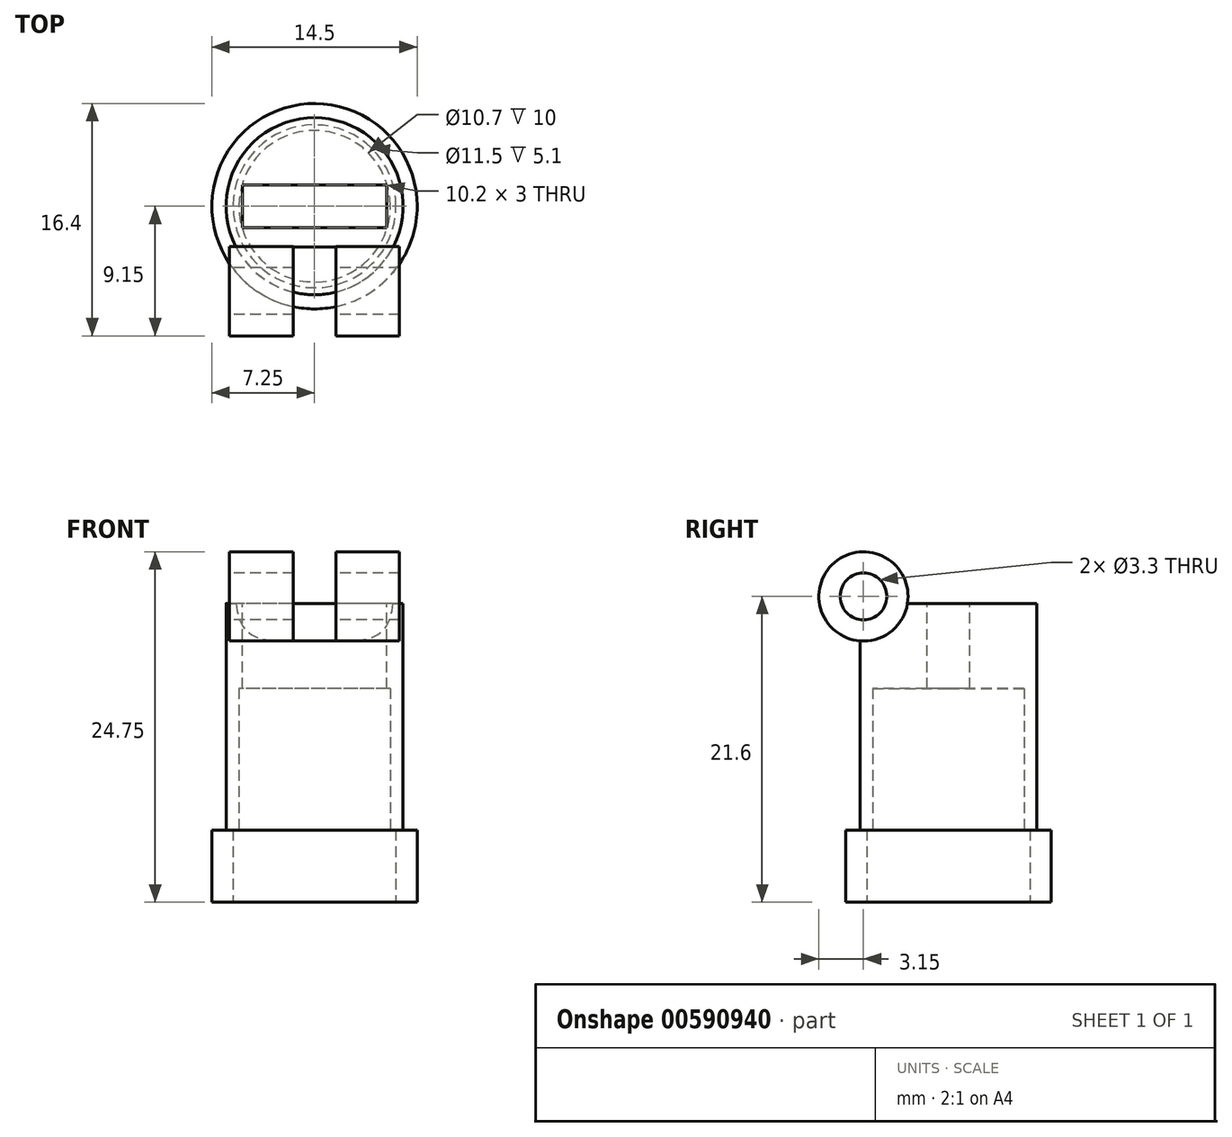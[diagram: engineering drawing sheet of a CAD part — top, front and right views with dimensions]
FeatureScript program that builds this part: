
annotation { "Feature Type Name" : "Feature", "Feature Type Description" : "" }
export const myFeature = defineFeature(function(context is Context, id is Id, definition is map)
    precondition{}
    {
        {
            var Q0;
            Q0=qCreatedBy(makeId("Top.planeOp"),FACE);
            var sketch = newSketch(context, id + "F0", { "sketchPlane" : qUnion([Q0])});
            skCircle(sketch, "E0", {"center": v(0, 0) * mm, "radius": 5.75 * mm});
            skCircle(sketch, "E1.0", {"center": v(0, 0) * mm, "radius": 7.25 * mm});
            skSolve(sketch);
        }
        {
            var Q0;
            Q0=makeQuery(id+"F0.imprint","IMPRINT",FACE,{"disambiguationData":[TD([[makeQuery(id+"F0.imprint","IMPRINT",EDGE,{"derivedFrom":sQuery(id+"F0.wireOp",EDGE,"E0")}),-1.0]])]});
            extrude(context, id + "F1", {"entities" : qUnion([Q0]), "depth" : 5.1 * mm, "offsetDistance" : 25 * mm});
        }
        {
            var Q0;
            Q0=makeQuery(id+"F1.opExtrude","CAP_FACE",FACE,{"disambiguationData":[OSD([sQuery(id+"F0.wireOp",EDGE,"E0"),sQuery(id+"F0.wireOp",EDGE,"E1.0")])],"isStart":false});
            var sketch = newSketch(context, id + "F2", { "sketchPlane" : qUnion([Q0])});
            skCircle(sketch, "E2.0", {"center": v(0, 0) * mm, "radius": 5.35 * mm});
            skCircle(sketch, "E3.0", {"center": v(0, 0) * mm, "radius": 6.25 * mm});
            skSolve(sketch);
        }
        {
            var Q0;
            Q0=makeQuery(id+"F2.imprint","IMPRINT",FACE,{"disambiguationData":[TD([[makeQuery(id+"F2.imprint","IMPRINT",EDGE,{"derivedFrom":sQuery(id+"F2.wireOp",EDGE,"E3.0")}),1.0]])]});
            var Q1;
            Q1=makeQuery(id+"F2.imprint","IMPRINT",FACE,{"disambiguationData":[TD([[makeQuery(id+"F2.imprint","IMPRINT",EDGE,{"derivedFrom":sQuery(id+"F2.wireOp",EDGE,"E2.0")}),-1.0]])]});
            extrude(context, id + "F3", {"entities" : qUnion([Q0, Q1]), "depth" : 16 * mm, "offsetDistance" : 25 * mm});
        }
        {
            var Q0;
            Q0=makeQuery(id+"F3.opExtrude","CAP_FACE",FACE,{"disambiguationData":[OSD([sQuery(id+"F0.wireOp",EDGE,"E0"),sQuery(id+"F2.wireOp",EDGE,"E2.0")])],"isStart":false});
            var sketch = newSketch(context, id + "F4", { "sketchPlane" : qUnion([Q0])});
            skCircle(sketch, "E4.0", {"center": v(0, 0) * mm, "radius": 0.6 * mm});
            skSolve(sketch);
        }
        {
            var Q0;
            Q0=makeQuery(id+"F4.imprint","IMPRINT",FACE,{"disambiguationData":[TD([[makeQuery(id+"F4.imprint","IMPRINT",EDGE,{"derivedFrom":sQuery(id+"F4.wireOp",EDGE,"E4.0")}),-1.0]])]});
            extrude(context, id + "F5", {"entities" : qUnion([Q0]), "operationType" : NewBodyOperationType.ADD, "oppositeDirection" : true, "depth" : 6 * mm, "offsetDistance" : 25 * mm});
        }
        {
            var Q0;
            {var subQ0=sQuery(id+"F2.wireOp",EDGE,"E2.0");Q0=makeQuery(id+"F5.boolean.opBoolean","MERGE",FACE,{"derivedFrom":[makeQuery(id+"F3.opExtrude","CAP_FACE",FACE,{"disambiguationData":[OSD([sQuery(id+"F0.wireOp",EDGE,"E0"),subQ0])],"isStart":false}),makeQuery(id+"F5.opExtrude","CAP_FACE",FACE,{"disambiguationData":[OSD([subQ0,sQuery(id+"F4.wireOp",EDGE,"E4.0")])],"isStart":true})]});}
            var sketch = newSketch(context, id + "F6", { "sketchPlane" : qUnion([Q0])});
            skLineSegment(sketch, "E5.bottom", {"start": v(5.1, 1.5) * mm, "end": v(-5.1, 1.5) * mm});
            skLineSegment(sketch, "E5.top", {"start": v(5.1, -1.5) * mm, "end": v(-5.1, -1.5) * mm});
            skLineSegment(sketch, "E5.left", {"start": v(5.1, 1.5) * mm, "end": v(5.1, -1.5) * mm});
            skLineSegment(sketch, "E5.right", {"start": v(-5.1, 1.5) * mm, "end": v(-5.1, -1.5) * mm});
            skPoint(sketch, "E5.middle", {"position": v(0, 0) * mm});
            skSolve(sketch);
        }
        {
            var Q0;
            Q0=makeQuery(id+"F6.imprint","IMPRINT",FACE,{"disambiguationData":[TD([[makeQuery(id+"F6.imprint","IMPRINT",EDGE,{"derivedFrom":sQuery(id+"F6.wireOp",EDGE,"E5.bottom")}),1.0]])]});
            extrude(context, id + "F7", {"entities" : qUnion([Q0]), "operationType" : NewBodyOperationType.REMOVE, "oppositeDirection" : true, "depth" : 10 * mm, "offsetDistance" : 25 * mm});
        }
        {
            var Q0;
            Q0=qCreatedBy(makeId("Right.planeOp"),FACE);
            var sketch = newSketch(context, id + "F8", { "sketchPlane" : qUnion([Q0])});
            skCircle(sketch, "E6", {"center": v(-6, 21.6) * mm, "radius": 3.15 * mm});
            skCircle(sketch, "E7", {"center": v(-6, 21.6) * mm, "radius": 1.65 * mm});
            skSolve(sketch);
        }
        {
            var Q0;
            Q0=makeQuery(id+"F8.imprint","IMPRINT",FACE,{"disambiguationData":[TD([[makeQuery(id+"F8.imprint","IMPRINT",EDGE,{"derivedFrom":sQuery(id+"F8.wireOp",EDGE,"E6")}),1.0]])]});
            extrude(context, id + "F9", {"entities" : qUnion([Q0]), "operationType" : NewBodyOperationType.ADD, "depth" : 6 * mm, "offsetDistance" : 25 * mm, "hasSecondDirection" : true, "secondDirectionOppositeDirection" : true, "secondDirectionDepth" : 6 * mm});
        }
        {
            var Q0;
            Q0 = qSketchRegion(id + "F8", true);
            extrude(context, id + "F10", {"entities" : qUnion([Q0]), "operationType" : NewBodyOperationType.REMOVE, "depth" : 1.5 * mm, "offsetDistance" : 25 * mm, "hasSecondDirection" : true, "secondDirectionOppositeDirection" : true, "secondDirectionDepth" : 1.5 * mm});
        }
        {
            var Q0;
            Q0=makeQuery(id+"F9.opExtrude","CAP_FACE",FACE,{"disambiguationData":[OSD([sQuery(id+"F8.wireOp",EDGE,"E6"),sQuery(id+"F8.wireOp",EDGE,"E7")])],"isStart":true});
            var sketch = newSketch(context, id + "F11", { "sketchPlane" : qUnion([Q0])});
            skCircle(sketch, "E8", {"center": v(6, 21.6) * mm, "radius": 1.65 * mm});
            skPoint(sketch, "E8.first.point", {"position": v(4.35, 21.55) * mm});
            skPoint(sketch, "E8.second.point", {"position": v(7.65, 21.7) * mm});
            skPoint(sketch, "E8.third.point", {"position": v(5.97, 23.25) * mm});
            skSolve(sketch);
        }
        {
            var Q0;
            Q0=makeQuery(id+"F11.imprint","IMPRINT",FACE,{"disambiguationData":[TD([[makeQuery(id+"F11.imprint","IMPRINT",EDGE,{"derivedFrom":sQuery(id+"F11.wireOp",EDGE,"E8")}),-1.0]])]});
            extrude(context, id + "F12", {"entities" : qUnion([Q0]), "operationType" : NewBodyOperationType.REMOVE, "oppositeDirection" : true, "depth" : 25 * mm, "offsetDistance" : 25 * mm});
        }
    });
